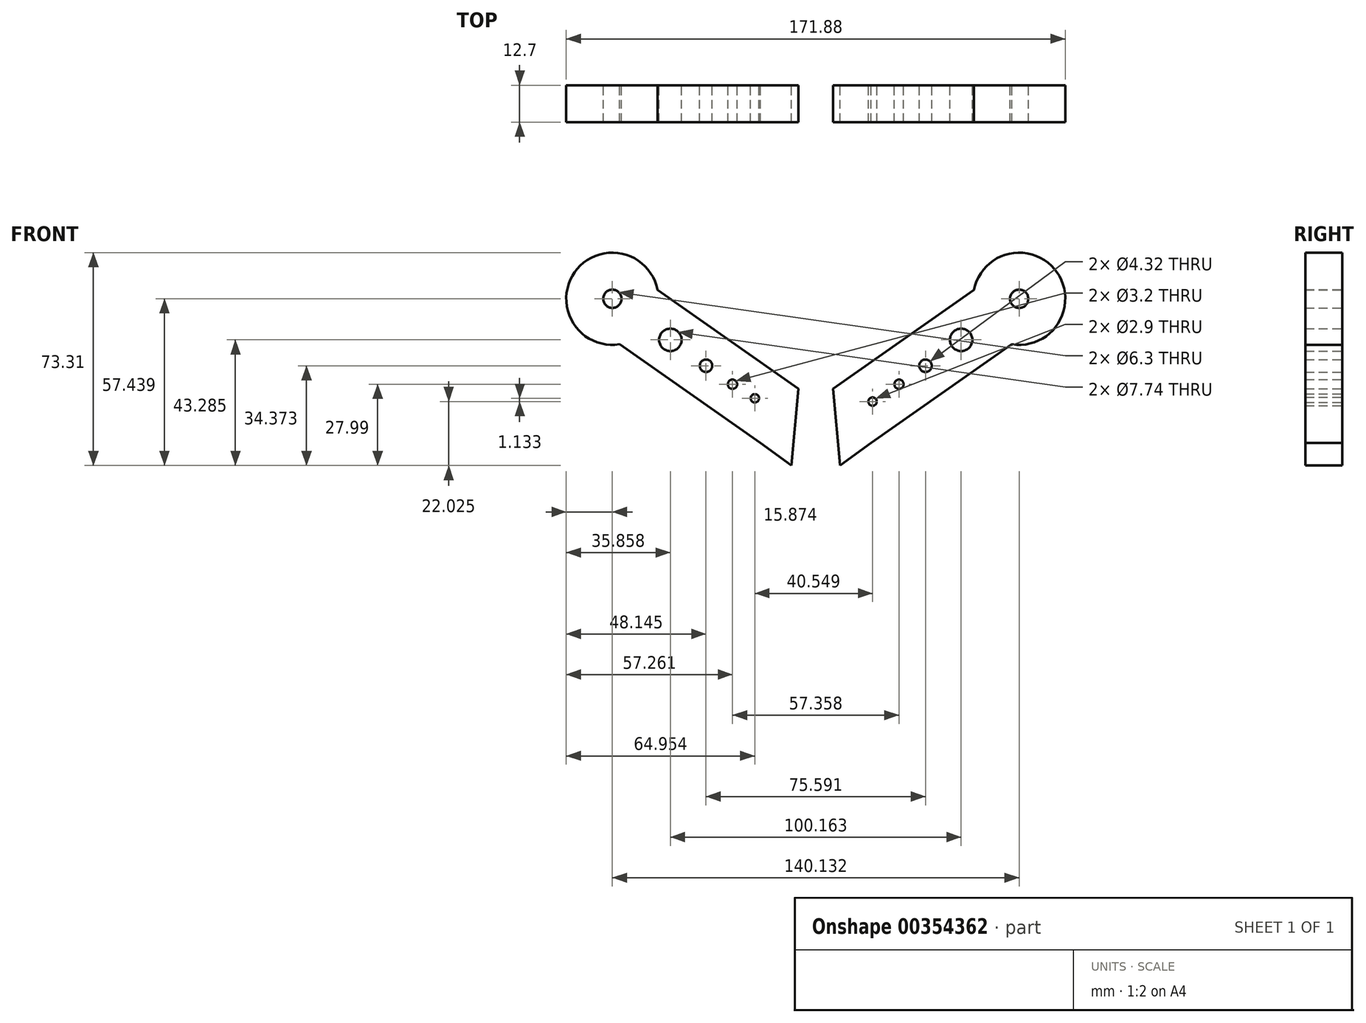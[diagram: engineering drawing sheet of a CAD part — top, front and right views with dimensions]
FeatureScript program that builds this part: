
annotation { "Feature Type Name" : "Feature", "Feature Type Description" : "" }
export const myFeature = defineFeature(function(context is Context, id is Id, definition is map)
    precondition{}
    {
        {
            var Q0;
            Q0=qCreatedBy(makeId("Front.planeOp"),FACE);
            var sketch = newSketch(context, id + "F0", { "sketchPlane" : qUnion([Q0])});
            skLineSegment(sketch, "E0.bottom", {"start": v(-5.96, 13.84) * mm, "end": v(-54.48, 47.8) * mm});
            skLineSegment(sketch, "E0.top", {"start": v(-19.07, -4.9) * mm, "end": v(-67.6, 29.08) * mm});
            skLineSegment(sketch, "E0.left", {"start": v(-5.96, 13.84) * mm, "end": v(-19.07, -4.9) * mm});
            skLineSegment(sketch, "E0.right", {"start": v(-54.48, 47.8) * mm, "end": v(-67.6, 29.08) * mm});
            skCircle(sketch, "E1", {"center": v(-70.07, 44.77) * mm, "radius": 15.88 * mm});
            skPoint(sketch, "E1.centerSnap0", {"position": v(-61.04, 38.45) * mm});
            skLineSegment(sketch, "E2", {"start": v(0, 76.66) * mm, "end": v(0, -76.54) * mm});
            skCircle(sketch, "E3", {"center": v(-50.08, 30.62) * mm, "radius": 3.87 * mm});
            skCircle(sketch, "E4", {"center": v(-37.8, 21.7) * mm, "radius": 2.16 * mm});
            skCircle(sketch, "E5", {"center": v(-28.68, 15.32) * mm, "radius": 1.6 * mm});
            skCircle(sketch, "E6", {"center": v(-70.07, 44.77) * mm, "radius": 3.15 * mm});
            skLineSegment(sketch, "E7", {"start": v(-8.33, -12.67) * mm, "end": v(-19.07, -4.9) * mm});
            skLineSegment(sketch, "E8", {"start": v(-8.33, -12.67) * mm, "end": v(-5.96, 13.84) * mm});
            skCircle(sketch, "E9.MirrorC", {"center": v(28.68, 15.32) * mm, "radius": 1.6 * mm});
            skLineSegment(sketch, "E10.MirrorCS", {"start": v(8.33, -12.67) * mm, "end": v(5.96, 13.84) * mm});
            skLineSegment(sketch, "E11.MirrorCS", {"start": v(8.33, -12.67) * mm, "end": v(19.07, -4.9) * mm});
            skCircle(sketch, "E12.MirrorC", {"center": v(70.07, 44.77) * mm, "radius": 3.15 * mm});
            skCircle(sketch, "E13.MirrorC", {"center": v(37.8, 21.7) * mm, "radius": 2.16 * mm});
            skCircle(sketch, "E14.MirrorC", {"center": v(50.08, 30.62) * mm, "radius": 3.87 * mm});
            skCircle(sketch, "E15.MirrorC", {"center": v(70.07, 44.77) * mm, "radius": 15.88 * mm});
            skLineSegment(sketch, "E16.MirrorCS", {"start": v(54.48, 47.8) * mm, "end": v(67.6, 29.08) * mm});
            skLineSegment(sketch, "E17.MirrorCS", {"start": v(5.96, 13.84) * mm, "end": v(19.07, -4.9) * mm});
            skLineSegment(sketch, "E18.MirrorCS", {"start": v(19.07, -4.9) * mm, "end": v(67.6, 29.08) * mm});
            skPoint(sketch, "E19.MirrorP", {"position": v(61.04, 38.45) * mm});
            skLineSegment(sketch, "E20.MirrorCS", {"start": v(5.96, 13.84) * mm, "end": v(54.48, 47.8) * mm});
            skCircle(sketch, "E21", {"center": v(-20.99, 10.49) * mm, "radius": 1.45 * mm});
            skCircle(sketch, "E22", {"center": v(19.56, 9.35) * mm, "radius": 1.45 * mm});
            skSolve(sketch);
        }
        {
            var Q0;
            Q0 = qSketchRegion(id + "F0", true);
            extrude(context, id + "F1", {"entities" : qUnion([Q0]), "endBound" : BoundingType.SYMMETRIC, "depth" : 12.7 * mm});
        }
    });
